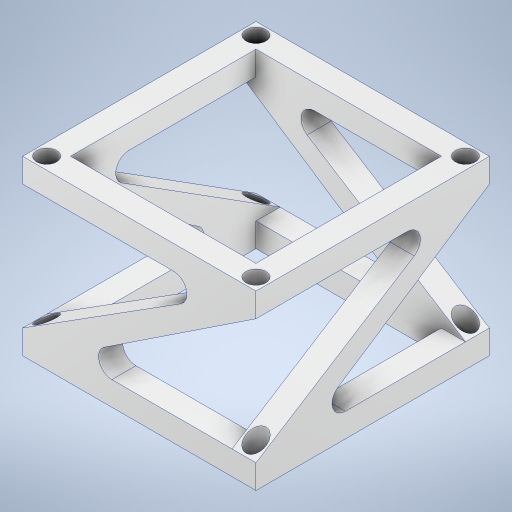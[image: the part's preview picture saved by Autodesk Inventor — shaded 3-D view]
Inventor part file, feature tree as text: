
AUTODESK INVENTOR PART (.ipt)
format: ipt  version: 2024 (Build 280153000, 153)  size: 395,264 bytes
history: native  units: in
note: dims shown in document units (in); Inventor stores cm internally (conversion verified against a paired STEP export)
features: extrude x5, sketch x5
ambient origin geometry x8: Origin, YZ Plane, XZ Plane, XY Plane, X Axis, Y Axis, Z Axis, Center Point
bodies: Solid1 (feature_tree)
feature tree (10):
  extrude  "Extrusion1"  Depth=1.378in
  extrude  "Extrusion2"  Depth=0.1417in
  sketch  "Sketch1"  dims[d0=1.378in d1=1.378in]
  sketch  "Sketch3"  dims[d2=0.1417in d3=0.1417in]
  sketch  "Sketch8"  dims[d4=0.1417in d5=0.1417in]
  sketch  "Sketch9"  dims[d6=0.1181in d7=0.0709in]
  sketch  "Sketch10"  dims[d8=0.0709in d9=0.1181in d10=0.0709in d11=0.0709in d12=0.1181in d13=0.0709in d14=0.0709in d15=0.1181in d16=0.0709in d17=0.0709in d22=1.0197in d23=0.0in d41=0.7091in d42=0.1575in d50=0.1417in d52=0.1417in d53=0.0in d67=0.1417in d70=0.1417in d71=0.1575in d75=0.1575in d76=0.1417in d77=0.1417in d78=0.1575in d79=0.1417in d80=0.7091in d82=0.0in d83=0.1417in d84=0.1575in d85=0.1417in d86=0.1417in d87=0.1575in d88=0.1417in d89=0.7091in d91=0.0in d92=0.1417in d93=0.1575in d94=0.1417in d95=0.1417in d96=0.1575in d97=0.1417in d98=0.7091in d100=0.0in d101=0.1417in]
  extrude  "Extrusion4"  Depth=0.1417in
  extrude  "Extrusion5"  Depth=0.0709in
  extrude  "Extrusion6"  Depth=0.1417in
